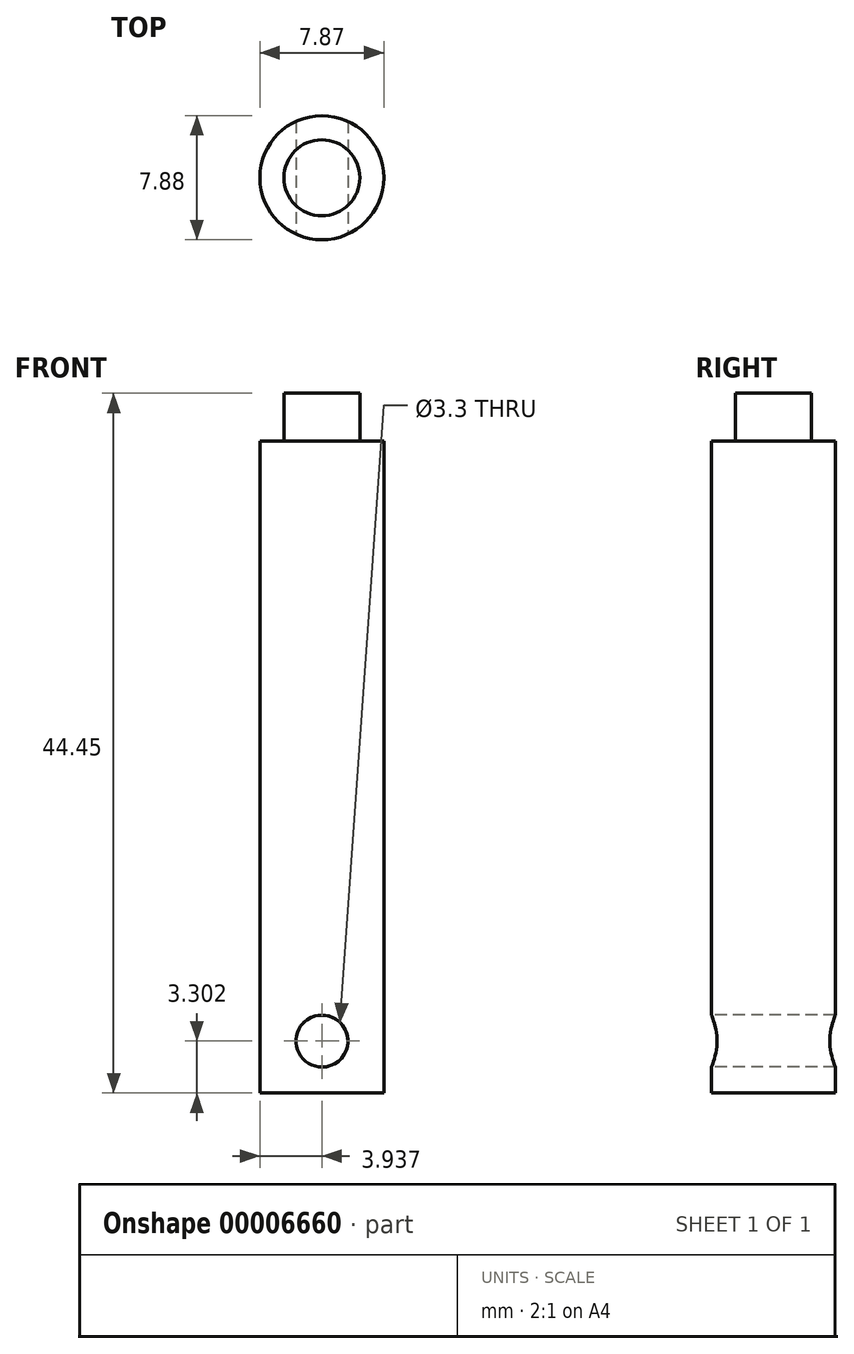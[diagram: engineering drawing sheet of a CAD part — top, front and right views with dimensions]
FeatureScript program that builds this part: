
annotation { "Feature Type Name" : "Feature", "Feature Type Description" : "" }
export const myFeature = defineFeature(function(context is Context, id is Id, definition is map)
    precondition{}
    {
        {
            var Q0;
            Q0=qCreatedBy(makeId("Top.planeOp"),FACE);
            var sketch = newSketch(context, id + "F0", { "sketchPlane" : qUnion([Q0])});
            skLineSegment(sketch, "E0", {"start": v(0, 0) * mm, "end": v(7.87, 0) * mm});
            skCircle(sketch, "E1", {"center": v(3.94, 0) * mm, "radius": 3.94 * mm});
            skSolve(sketch);
        }
        {
            var Q0;
            Q0 = qSketchRegion(id + "F0", true);
            extrude(context, id + "F1", {"entities" : qUnion([Q0]), "depth" : 41.4 * mm});
        }
        {
            var Q0;
            Q0=makeQuery(id+"F1.opExtrude","CAP_FACE",FACE,{"disambiguationData":[OSD([sQuery(id+"F0.wireOp",EDGE,"E1")])],"isStart":false});
            var sketch = newSketch(context, id + "F2", { "sketchPlane" : qUnion([Q0])});
            skCircle(sketch, "E2", {"center": v(3.94, 0) * mm, "radius": 2.41 * mm});
            skSolve(sketch);
        }
        {
            var Q0;
            Q0 = qSketchRegion(id + "F2", true);
            extrude(context, id + "F3", {"entities" : qUnion([Q0]), "operationType" : NewBodyOperationType.ADD, "depth" : 3.05 * mm});
        }
        {
            var Q0;
            Q0=qCreatedBy(makeId("Front.planeOp"),FACE);
            var sketch = newSketch(context, id + "F4", { "sketchPlane" : qUnion([Q0])});
            skLineSegment(sketch, "E3", {"start": v(0, 0) * mm, "end": v(0, 3.3) * mm});
            skLineSegment(sketch, "E4", {"start": v(0, 3.3) * mm, "end": v(3.94, 3.3) * mm});
            skCircle(sketch, "E5", {"center": v(3.94, 3.3) * mm, "radius": 1.65 * mm});
            skSolve(sketch);
        }
        {
            var Q0;
            Q0 = qSketchRegion(id + "F4", true);
            extrude(context, id + "F5", {"entities" : qUnion([Q0]), "operationType" : NewBodyOperationType.REMOVE, "oppositeDirection" : true, "depth" : 25.4 * mm});
        }
        {
            var Q0;
            Q0 = qSketchRegion(id + "F4", true);
            extrude(context, id + "F6", {"entities" : qUnion([Q0]), "operationType" : NewBodyOperationType.REMOVE, "depth" : 25.4 * mm});
        }
    });
